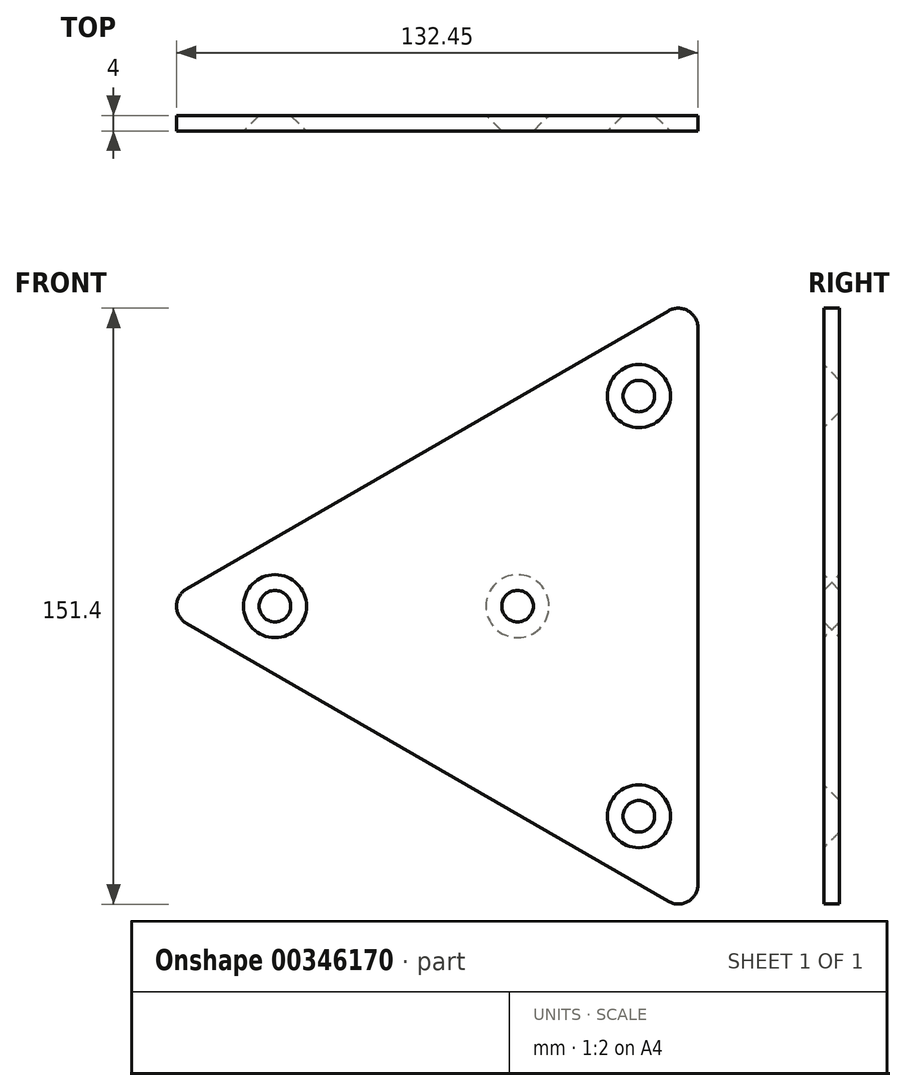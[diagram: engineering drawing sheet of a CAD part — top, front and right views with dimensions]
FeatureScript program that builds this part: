
annotation { "Feature Type Name" : "Feature", "Feature Type Description" : "" }
export const myFeature = defineFeature(function(context is Context, id is Id, definition is map)
    precondition{}
    {
        {
            var Q0;
            Q0=qCreatedBy(makeId("Front.planeOp"),FACE);
            var sketch = newSketch(context, id + "F0", { "sketchPlane" : qUnion([Q0])});
            skCircle(sketch, "E0.cCircle", {"center": v(0, 0) * mm, "radius": 45.82 * mm, "construction": true});
            skLineSegment(sketch, "E0.0", {"start": v(45.82, 79.36) * mm, "end": v(45.82, -79.36) * mm});
            skLineSegment(sketch, "E0.1", {"start": v(45.82, -79.36) * mm, "end": v(-91.63, 0) * mm});
            skLineSegment(sketch, "E0.2", {"start": v(-91.63, 0) * mm, "end": v(45.82, 79.36) * mm});
            skPoint(sketch, "E0.0.midPoint", {"position": v(45.82, 0) * mm});
            skLineSegment(sketch, "E1", {"start": v(45.82, 79.36) * mm, "end": v(-22.9, -39.68) * mm, "construction": true});
            skLineSegment(sketch, "E2", {"start": v(-91.63, 0) * mm, "end": v(45.82, 0) * mm, "construction": true});
            skLineSegment(sketch, "E3", {"start": v(45.82, -79.36) * mm, "end": v(-22.9, 39.68) * mm, "construction": true});
            skCircle(sketch, "E4", {"center": v(30.82, 53.38) * mm, "radius": 16 * mm, "construction": true});
            skCircle(sketch, "E5", {"center": v(30.82, 53.38) * mm, "radius": 3 * mm});
            skCircle(sketch, "E6", {"center": v(-61.63, 0) * mm, "radius": 3 * mm});
            skCircle(sketch, "E7", {"center": v(30.82, -53.38) * mm, "radius": 3 * mm});
            skCircle(sketch, "E8", {"center": v(0, 0) * mm, "radius": 3 * mm});
            skSolve(sketch);
        }
        {
            var Q0;
            Q0=makeQuery(id+"F0.imprint","IMPRINT",FACE,{"disambiguationData":[TD([[makeQuery(id+"F0.imprint","IMPRINT",EDGE,{"derivedFrom":sQuery(id+"F0.wireOp",EDGE,"E0.0")}),-1.0]])]});
            extrude(context, id + "F1", {"entities" : qUnion([Q0]), "depth" : 4 * mm});
        }
        {
            var Q0;
            Q0=makeQuery(id+"F1.opExtrude","SWEPT_EDGE",EDGE,{"disambiguationData":[OSD([sQuery(id+"F0.wireOp",EDGE,"E0.0"),sQuery(id+"F0.wireOp",EDGE,"E0.2")])]});
            var Q1;
            Q1=makeQuery(id+"F1.opExtrude","SWEPT_EDGE",EDGE,{"disambiguationData":[OSD([sQuery(id+"F0.wireOp",EDGE,"E0.0"),sQuery(id+"F0.wireOp",EDGE,"E0.1")])]});
            var Q2;
            Q2=makeQuery(id+"F1.opExtrude","SWEPT_EDGE",EDGE,{"disambiguationData":[OSD([sQuery(id+"F0.wireOp",EDGE,"E0.1"),sQuery(id+"F0.wireOp",EDGE,"E0.2")])]});
            fillet(context, id + "F2", {"entities" : qUnion([Q0, Q1, Q2]), "radius" : 5 * mm, "tangentPropagation" : true, "allowEdgeOverflow" : false});
        }
        {
            var Q0;
            Q0=makeQuery(id+"F1.opExtrude","CAP_EDGE",EDGE,{"disambiguationData":[OSD([sQuery(id+"F0.wireOp",EDGE,"E8")])],"isStart":true});
            var Q1;
            Q1=makeQuery(id+"F1.opExtrude","CAP_EDGE",EDGE,{"disambiguationData":[OSD([sQuery(id+"F0.wireOp",EDGE,"E6")])],"isStart":false});
            var Q2;
            Q2=makeQuery(id+"F1.opExtrude","CAP_EDGE",EDGE,{"disambiguationData":[OSD([sQuery(id+"F0.wireOp",EDGE,"E5")])],"isStart":false});
            var Q3;
            Q3=makeQuery(id+"F1.opExtrude","CAP_EDGE",EDGE,{"disambiguationData":[OSD([sQuery(id+"F0.wireOp",EDGE,"E7")])],"isStart":false});
            chamfer(context, id + "F3", {"entities" : qUnion([Q0, Q1, Q2, Q3]), "width" : 5 * mm, "tangentPropagation" : true});
        }
    });
